# Revit family: BNB4
name_source: partatom
category: Lighting Fixtures
units: mm (PartAtom-declared; Revit-internal decimal feet)

## family parameters
Always vertical = Yes
Cut with Voids When Loaded = No
Light Source = Yes
OmniClass Number = 23.80.70.14.11
OmniClass Title = Amenity Lighting
Part Type = Normal
Room Calculation Point = No
Round Connector Dimension = Use Diameter
Shared = No
Work Plane-Based = No

## types (1)
- BNB4
    Apparent Load = 0 VA
    Assembly Code = D5020200
    Body Material = Metal-Aluminum Alloy
    Color Filter = 16777215
    Default Elevation = 0"
    Description = Low Level Luminaire
    Dimming Lamp Color Temperature Shift = <None>
    Emit Shape Visible in Rendering = No
    Emit from Circle Diameter = 6"
    Finish = All colors shall be a Super TGIC thermoset polyester powder coat paint
    Full Load Current = 0 A
    Glass Material = Glass-Clear
    Housing Material = Metal-Aluminum Alloy
    Initial Lumens = 0 lm
    Lamp = LED
    Lighting Source Height = 38"
    Load Classification = Lighting
    Manufacturer = Kim Lighting
    MasterFormat Title = Landscape Lighting, Site Lighting, Walkway Lighting
    Model = Bounce Bollard
    Note Text = LF
    Note Visible = Yes
    Number of Poles = 1
    Photometric Notes = More IES files download on Photometric Web Link
    Photometric Web File = bnb-18l3k.ies
    Power Factor = 1
    Series = Bounce Bollard Luminaire
    Tilt Angle = 90.00°
    Type Comments = Lighting Fixture
    URL = https://www.currentlighting.com
    Voltage = 208 V
    Wattage Comments = 21,31 & 41 Watts

## geometry (parser evidence)
native form markers: Blend x12, Sweep x3
no freeform markers — native parametric forms only
